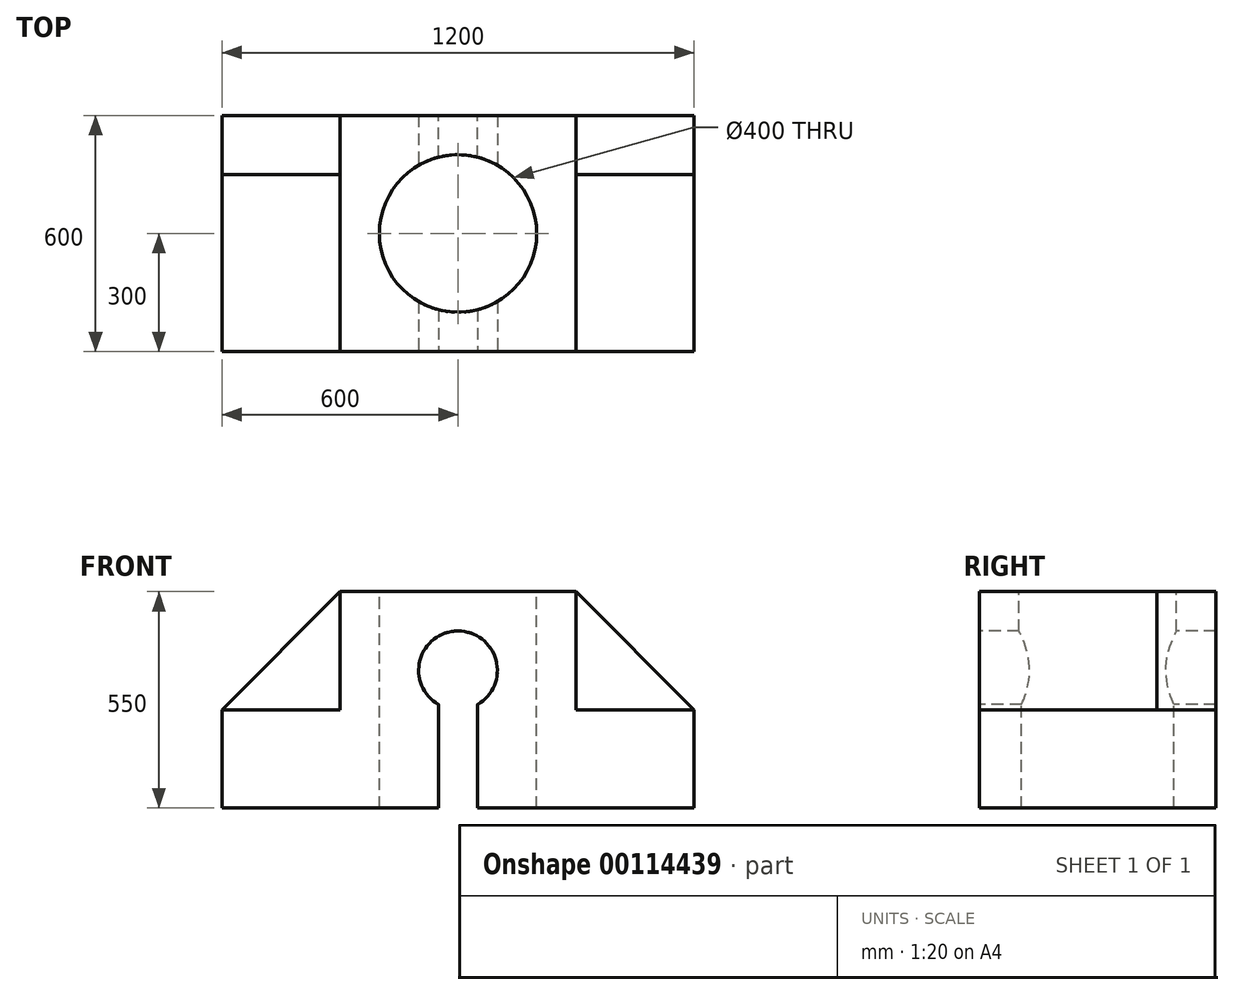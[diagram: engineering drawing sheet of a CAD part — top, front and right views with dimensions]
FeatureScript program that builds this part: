
annotation { "Feature Type Name" : "Feature", "Feature Type Description" : "" }
export const myFeature = defineFeature(function(context is Context, id is Id, definition is map)
    precondition{}
    {
        {
            var Q0;
            Q0=qCreatedBy(makeId("Top.planeOp"),FACE);
            var sketch = newSketch(context, id + "F0", { "sketchPlane" : qUnion([Q0])});
            skLineSegment(sketch, "E0.bottom", {"start": v(-600, -300) * mm, "end": v(600, -300) * mm});
            skLineSegment(sketch, "E0.top", {"start": v(-600, 300) * mm, "end": v(600, 300) * mm});
            skLineSegment(sketch, "E0.left", {"start": v(-600, -300) * mm, "end": v(-600, 300) * mm});
            skLineSegment(sketch, "E0.right", {"start": v(600, -300) * mm, "end": v(600, 300) * mm});
            skPoint(sketch, "E0.middle", {"position": v(0, 0) * mm});
            skSolve(sketch);
        }
        {
            var Q0;
            Q0 = qSketchRegion(id + "F0", true);
            extrude(context, id + "F1", {"entities" : qUnion([Q0]), "depth" : 250 * mm});
        }
        {
            var Q0;
            Q0=makeQuery(id+"F1.opExtrude","CAP_FACE",FACE,{"disambiguationData":[OSD([sQuery(id+"F0.wireOp",EDGE,"E0.bottom"),sQuery(id+"F0.wireOp",EDGE,"E0.top"),sQuery(id+"F0.wireOp",EDGE,"E0.left"),sQuery(id+"F0.wireOp",EDGE,"E0.right")])],"isStart":false});
            var sketch = newSketch(context, id + "F2", { "sketchPlane" : qUnion([Q0])});
            skLineSegment(sketch, "E1.bottom", {"start": v(-300, 300) * mm, "end": v(300, 300) * mm});
            skLineSegment(sketch, "E1.top", {"start": v(-300, -300) * mm, "end": v(300, -300) * mm});
            skLineSegment(sketch, "E1.left", {"start": v(-300, 300) * mm, "end": v(-300, -300) * mm});
            skLineSegment(sketch, "E1.right", {"start": v(300, 300) * mm, "end": v(300, -300) * mm});
            skPoint(sketch, "E1.middle", {"position": v(0, 0) * mm});
            skSolve(sketch);
        }
        {
            var Q0;
            Q0 = qSketchRegion(id + "F2", true);
            extrude(context, id + "F3", {"entities" : qUnion([Q0]), "operationType" : NewBodyOperationType.ADD, "depth" : 300 * mm});
        }
        {
            var Q0;
            Q0=makeQuery(id+"F3.boolean.opBoolean","MERGE",FACE,{"derivedFrom":[makeQuery(id+"F1.opExtrude","SWEPT_FACE",FACE,{"disambiguationData":[OSD([sQuery(id+"F0.wireOp",EDGE,"E0.bottom")])]}),makeQuery(id+"F3.opExtrude","SWEPT_FACE",FACE,{"disambiguationData":[OSD([sQuery(id+"F2.wireOp",EDGE,"E1.top")])]})]});
            var sketch = newSketch(context, id + "F4", { "sketchPlane" : qUnion([Q0])});
            skLineSegment(sketch, "E2.bottom", {"start": v(-50, -350) * mm, "end": v(50, -350) * mm});
            skLineSegment(sketch, "E2.left", {"start": v(-50, -350) * mm, "end": v(-50, 263.4) * mm});
            skLineSegment(sketch, "E2.right", {"start": v(50, -350) * mm, "end": v(50, 263.4) * mm});
            skPoint(sketch, "E2.middle", {"position": v(0, 0) * mm});
            skArc(sketch, "E3", {"start": v(50, 263.4) * mm, "mid": v(0, 450) * mm, "end": v(-50, 263.4) * mm});
            skPoint(sketch, "E4.orphan", {"position": v(50, 350) * mm});
            skPoint(sketch, "E5.orphan", {"position": v(-50, 350) * mm});
            skSolve(sketch);
        }
        {
            var Q0;
            Q0 = qSketchRegion(id + "F4", true);
            extrude(context, id + "F5", {"entities" : qUnion([Q0]), "operationType" : NewBodyOperationType.REMOVE, "endBound" : BoundingType.THROUGH_ALL, "oppositeDirection" : true, "depth" : 25 * mm});
        }
        {
            var Q0;
            Q0=makeQuery(id+"F3.opExtrude","CAP_FACE",FACE,{"disambiguationData":[OSD([sQuery(id+"F2.wireOp",EDGE,"E1.bottom"),sQuery(id+"F2.wireOp",EDGE,"E1.top"),sQuery(id+"F2.wireOp",EDGE,"E1.left"),sQuery(id+"F2.wireOp",EDGE,"E1.right")])],"isStart":false});
            var sketch = newSketch(context, id + "F6", { "sketchPlane" : qUnion([Q0])});
            skCircle(sketch, "E6", {"center": v(0, 0) * mm, "radius": 200 * mm});
            skSolve(sketch);
        }
        {
            var Q0;
            Q0 = qSketchRegion(id + "F6", true);
            extrude(context, id + "F7", {"entities" : qUnion([Q0]), "operationType" : NewBodyOperationType.REMOVE, "endBound" : BoundingType.THROUGH_ALL, "oppositeDirection" : true, "depth" : 25 * mm});
        }
        {
            var Q0;
            Q0=makeQuery(id+"F3.boolean.opBoolean","MERGE",FACE,{"derivedFrom":[makeQuery(id+"F1.opExtrude","SWEPT_FACE",FACE,{"disambiguationData":[OSD([sQuery(id+"F0.wireOp",EDGE,"E0.top")])]}),makeQuery(id+"F3.opExtrude","SWEPT_FACE",FACE,{"disambiguationData":[OSD([sQuery(id+"F2.wireOp",EDGE,"E1.bottom")])]})]});
            var sketch = newSketch(context, id + "F8", { "sketchPlane" : qUnion([Q0])});
            skLineSegment(sketch, "E7", {"start": v(-300, 550) * mm, "end": v(-600, 250) * mm});
            skLineSegment(sketch, "E8", {"start": v(-600, 250) * mm, "end": v(-300, 250) * mm});
            skLineSegment(sketch, "E9", {"start": v(-300, 250) * mm, "end": v(-300, 550) * mm});
            skLineSegment(sketch, "E10", {"start": v(300, 550) * mm, "end": v(600, 250) * mm});
            skLineSegment(sketch, "E11", {"start": v(600, 250) * mm, "end": v(300, 250) * mm});
            skLineSegment(sketch, "E12", {"start": v(300, 250) * mm, "end": v(300, 550) * mm});
            skSolve(sketch);
        }
        {
            var Q0;
            Q0 = qSketchRegion(id + "F8", true);
            extrude(context, id + "F9", {"entities" : qUnion([Q0]), "operationType" : NewBodyOperationType.ADD, "oppositeDirection" : true, "depth" : 150 * mm});
        }
    });
